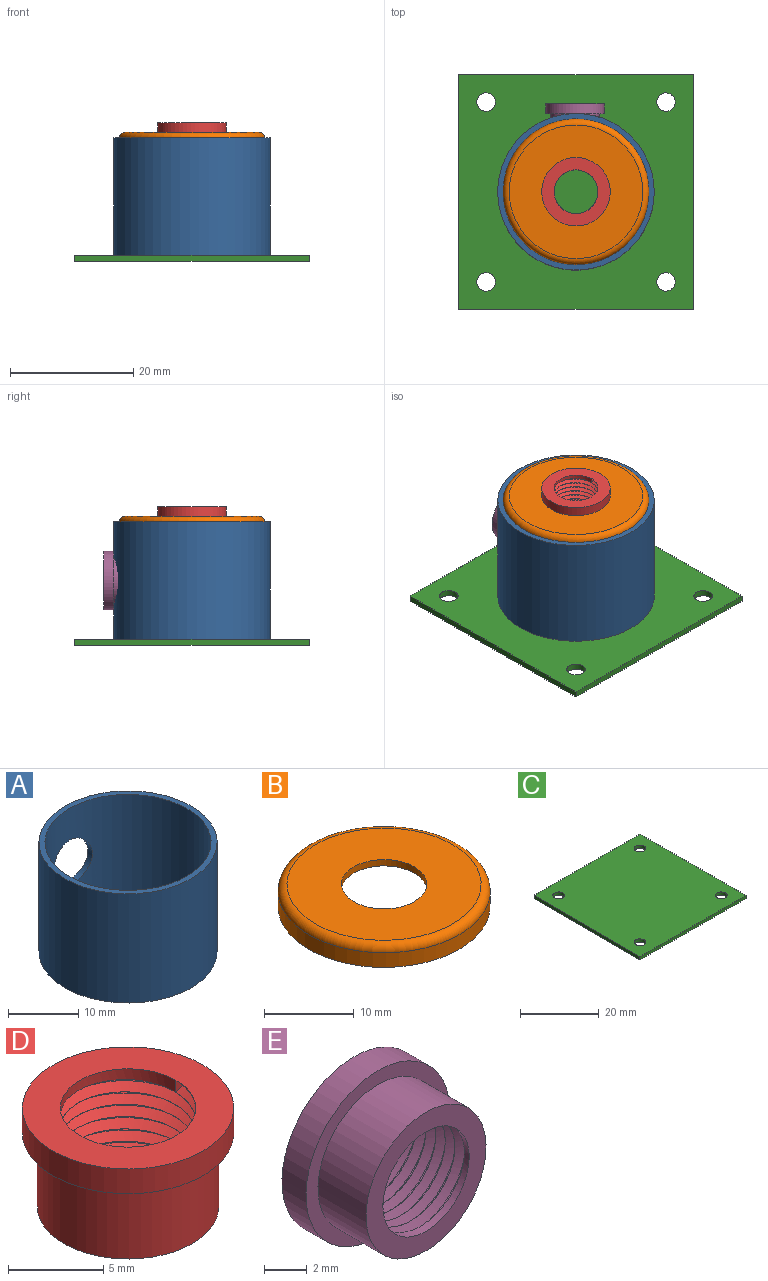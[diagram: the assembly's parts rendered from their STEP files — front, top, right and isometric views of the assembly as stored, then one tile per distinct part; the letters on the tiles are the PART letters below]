
ASSEMBLY  parts=5 mates=4
PART A: 5 faces, bbox 25.4x25.4x19.1 mm
  f0: cylinder r=11.84mm len=23.67mm, axis (0,0,-1), area 1366.6mm2, adj f2,f3,f4
  f1: cylinder r=12.7mm len=25.4mm, axis (0,0,-1), area 1470.1mm2, adj f2,f3,f4
  f2: plane 25.4x25.4mm, normal (0,0,1), area 66.6mm2, adj f0,f1
  f3: plane 25.4x25.4mm, normal (0,0,-1), area 66.6mm2, adj f0,f1
  f4: cylinder r=3.97mm len=7.94mm, axis (0,-1,0), area 22.1mm2, adj f0,f1
PART B: 8 faces, bbox 25.6x25.6x3 mm
  f0: cylinder r=4.76mm len=9.53mm, axis (0,0,1), area 25.8mm2, adj f1,f7
  f1: plane 21.18x21.18mm, normal (0,0,-1), area 281.2mm2, adj f0,f2
  f2: torus R=10.59mm, axis (0,0,1), area 40.7mm2, adj f1,f3
  f3: cylinder r=10.97mm len=21.95mm, axis (0,0,1), area 121mm2, adj f2,f4
  f4: plane 23.67x23.67mm, normal (0,0,-1), area 61.9mm2, adj f3,f5
  f5: cylinder r=11.84mm len=23.67mm, axis (0,0,1), area 148.7mm2, adj f4,f6
  f6: torus R=10.84mm, axis (0,0,1), area 113.2mm2, adj f5,f7
  f7: plane 21.67x21.67mm, normal (0,0,1), area 297.7mm2, adj f0,f6
PART C: 10 faces, bbox 38.1x38.1x1 mm
  f0: plane 38.1x1mm, normal (0,1,0), area 38.1mm2, adj f1,f7,f8,f9
  f1: plane 38.1x1mm, normal (-1,0,0), area 38.1mm2, adj f0,f2,f8,f9
  f2: plane 38.1x1mm, normal (0,-1,0), area 38.1mm2, adj f1,f7,f8,f9
  f3: cylinder r=1.5mm len=3mm, axis (0,0,-1), area 9.4mm2, adj f8,f9
  f4: cylinder r=1.5mm len=3mm, axis (0,0,-1), area 9.4mm2, adj f8,f9
  f5: cylinder r=1.5mm len=3mm, axis (0,0,-1), area 9.4mm2, adj f8,f9
  f6: cylinder r=1.5mm len=3mm, axis (0,0,-1), area 9.4mm2, adj f8,f9
  f7: plane 38.1x1mm, normal (1,0,0), area 38.1mm2, adj f0,f2,f8,f9
  f8: plane 38.1x38.1mm, normal (0,0,1), area 1423.3mm2, adj f0,f1,f2,f3,f4,f5,f6,f7
  f9: plane 38.1x38.1mm, normal (0,0,-1), area 1423.3mm2, adj f0,f1,f2,f3,f4,f5,f6,f7
PART D: 10 faces, bbox 11.5x11.5x7.1 mm
  f0: cylinder r=3.56mm len=7.12mm, axis (0,0,1), area 16.4mm2, adj f1,f2,f6,f8,f9
  f1: plane 11.11x11.11mm, normal (0,0,1), area 57.1mm2, adj f0,f5
  f2: plane 9.91x9.91mm, normal (0,0,-1), area 22.7mm2, adj f0,f3,f6,f7,f8
  f3: cylinder r=4.76mm len=9.53mm, axis (0,0,1), area 142.5mm2, adj f2,f4
  f4: plane 11.11x11.11mm, normal (0,0,-1), area 25.7mm2, adj f3,f5
  f5: cylinder r=5.56mm len=11.11mm, axis (0,0,1), area 55.4mm2, adj f1,f4
  f6: bspline ~9.54x8.27mm, area 119.8mm2, adj f0,f2,f7,f9
  f7: bspline ~9.76x8.45mm, area 47mm2, adj f2,f6,f8,f9
  f8: bspline ~9.55x8.27mm, area 114.1mm2, adj f0,f2,f7,f9
  f9: plane 0.8x0.64mm, normal (0,-1,0), area 0.3mm2, adj f0,f6,f7,f8
PART E: 10 faces, bbox 9.8x5.5x9.8 mm
  f0: cylinder r=2.85mm len=5.7mm, axis (0,-1,0), area 6.3mm2, adj f1,f5,f6,f8,f9
  f1: plane 7.94x7.94mm, normal (0,-1,0), area 24mm2, adj f0,f2
  f2: cylinder r=3.97mm len=7.94mm, axis (0,-1,0), area 79.2mm2, adj f1,f3
  f3: plane 9.53x9.53mm, normal (0,-1,0), area 21.8mm2, adj f2,f4
  f4: cylinder r=4.76mm len=9.53mm, axis (0,-1,0), area 47.5mm2, adj f3,f5
  f5: plane 9.81x9.81mm, normal (0,1,0), area 40.2mm2, adj f0,f4,f6,f7,f8
  f6: bspline ~7.64x6.62mm, area 72.8mm2, adj f0,f5,f7,f9
  f7: bspline ~7.8x6.76mm, area 27.8mm2, adj f5,f6,f8,f9
  f8: bspline ~7.64x6.62mm, area 67.4mm2, adj f0,f5,f7,f9
  f9: plane 0.64x0.51mm, normal (0,0,1), area 0.2mm2, adj f0,f6,f7,f8
PLACE A t=(0.9,-16.29,3.34)mm
PLACE B t=(0.9,-16.29,-18.85)mm
PLACE C t=(0.9,-16.29,27.34)mm
PLACE D t=(0.9,-16.29,-31.07)mm
PLACE E t=(0.72,-37.75,4.32)mm
MATE fastened B.f0 <-> D.f0  axis (0,0,1) through (0.9,-16.29,23.25)mm
MATE fastened A.f0 <-> B.f0  axis (0,0,-1) through (0.9,-16.29,22.39)mm
MATE fastened C.f8 <-> A.f0  axis (0,0,1) through (0.9,-16.29,3.34)mm
MATE fastened A.f4 <-> E.f3  axis (0,-1,0) through (0.9,-3.57,12.86)mm
